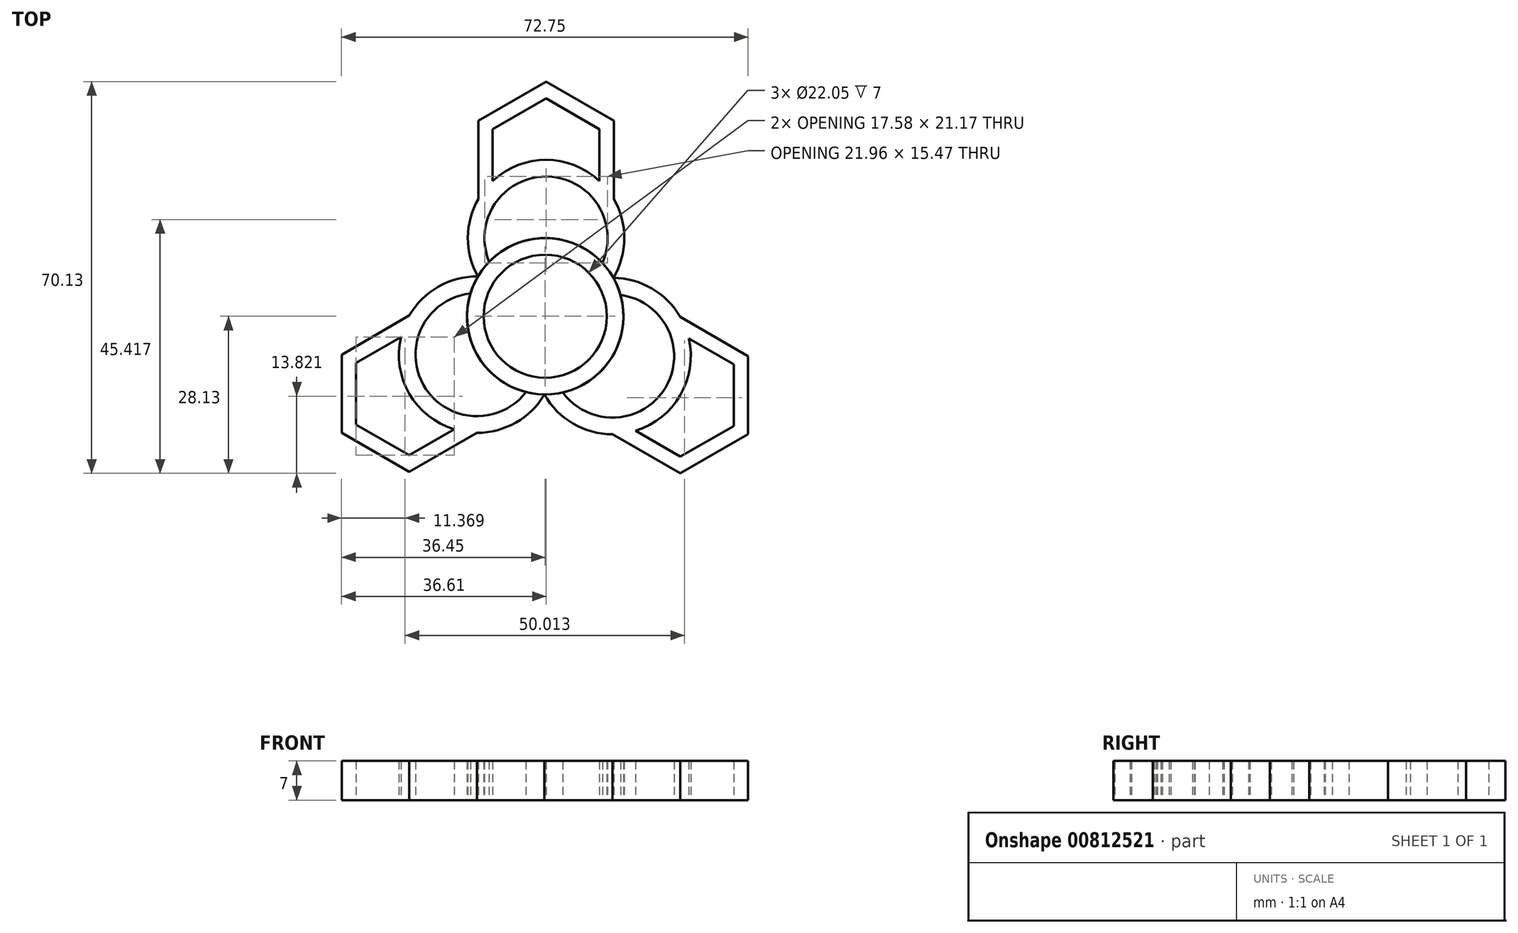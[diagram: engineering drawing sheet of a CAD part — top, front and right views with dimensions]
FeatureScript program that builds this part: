
annotation { "Feature Type Name" : "Feature", "Feature Type Description" : "" }
export const myFeature = defineFeature(function(context is Context, id is Id, definition is map)
    precondition{}
    {
        {
            var Q0;
            Q0=qCreatedBy(makeId("Top.planeOp"),FACE);
            var sketch = newSketch(context, id + "F0", { "sketchPlane" : qUnion([Q0])});
            skCircle(sketch, "E0", {"center": v(0, 0) * mm, "radius": 11.02 * mm});
            skCircle(sketch, "E1", {"center": v(0, 0) * mm, "radius": 14 * mm});
            skCircle(sketch, "E2", {"center": v(0.15, 14) * mm, "radius": 14 * mm});
            skCircle(sketch, "E3", {"center": v(0.15, 14) * mm, "radius": 11.02 * mm});
            skCircle(sketch, "E4.cCircle", {"center": v(0.15, 28) * mm, "radius": 14 * mm, "construction": true});
            skLineSegment(sketch, "E4.0", {"start": v(0.15, 14) * mm, "end": v(-11.98, 21) * mm});
            skLineSegment(sketch, "E4.1", {"start": v(-11.98, 21) * mm, "end": v(-11.98, 35) * mm});
            skLineSegment(sketch, "E4.2", {"start": v(-11.98, 35) * mm, "end": v(0.15, 42) * mm});
            skLineSegment(sketch, "E4.3", {"start": v(0.15, 42) * mm, "end": v(12.27, 35) * mm});
            skLineSegment(sketch, "E4.4", {"start": v(12.27, 35) * mm, "end": v(12.27, 21) * mm});
            skLineSegment(sketch, "E4.5", {"start": v(12.27, 21) * mm, "end": v(0.15, 14) * mm});
            skCircle(sketch, "E5.cCircle", {"center": v(0.15, 28) * mm, "radius": 11.02 * mm, "construction": true});
            skLineSegment(sketch, "E5.0", {"start": v(0.15, 39.02) * mm, "end": v(9.7, 33.51) * mm});
            skLineSegment(sketch, "E5.1", {"start": v(9.7, 33.51) * mm, "end": v(9.7, 22.49) * mm});
            skLineSegment(sketch, "E5.2", {"start": v(9.7, 22.49) * mm, "end": v(0.15, 16.98) * mm});
            skLineSegment(sketch, "E5.3", {"start": v(0.15, 16.98) * mm, "end": v(-9.4, 22.49) * mm});
            skLineSegment(sketch, "E5.4", {"start": v(-9.4, 22.49) * mm, "end": v(-9.4, 33.51) * mm});
            skLineSegment(sketch, "E5.5", {"start": v(-9.4, 33.51) * mm, "end": v(0.15, 39.02) * mm});
            skSolve(sketch);
        }
        {
            var Q0;
            {var subQ0=sQuery(id+"F0.wireOp",EDGE,"E2");var subQ1=sQuery(id+"F0.wireOp",EDGE,"E0");var subQ2=makeQuery(id+"F0.imprint","INTERSECT",VERTEX,{"disambiguationData":[OD(0.0)],"derivedFrom":[subQ1,subQ0]});Q0=makeQuery(id+"F0.imprint","IMPRINT",FACE,{"disambiguationData":[TD([[makeQuery(id+"F0.imprint","IMPRINT",EDGE,{"disambiguationData":[TD([[subQ2,1.0]])],"derivedFrom":subQ1}),-1.0]])]});}
            var Q1;
            {var subQ2=sQuery(id+"F0.wireOp",EDGE,"E3");var subQ4=sQuery(id+"F0.wireOp",EDGE,"E0");var subQ7=makeQuery(id+"F0.imprint","INTERSECT",VERTEX,{"disambiguationData":[OD(0.0)],"derivedFrom":[subQ4,subQ2]});Q1=makeQuery(id+"F0.imprint","IMPRINT",FACE,{"disambiguationData":[TD([[makeQuery(id+"F0.imprint","IMPRINT",EDGE,{"disambiguationData":[TD([[subQ7,-1.0]])],"derivedFrom":subQ4}),-1.0]])]});}
            var Q2;
            {var subQ0=sQuery(id+"F0.wireOp",EDGE,"E3");var subQ1=sQuery(id+"F0.wireOp",EDGE,"E0");var subQ2=makeQuery(id+"F0.imprint","INTERSECT",VERTEX,{"disambiguationData":[OD(1.0)],"derivedFrom":[subQ1,subQ0]});Q2=makeQuery(id+"F0.imprint","IMPRINT",FACE,{"disambiguationData":[TD([[makeQuery(id+"F0.imprint","IMPRINT",EDGE,{"disambiguationData":[TD([[subQ2,-1.0]])],"derivedFrom":subQ1}),-1.0]])]});}
            var Q3;
            {var subQ0=sQuery(id+"F0.wireOp",EDGE,"E3");var subQ1=sQuery(id+"F0.wireOp",EDGE,"E0");var subQ2=makeQuery(id+"F0.imprint","INTERSECT",VERTEX,{"disambiguationData":[OD(0.0)],"derivedFrom":[subQ1,subQ0]});Q3=makeQuery(id+"F0.imprint","IMPRINT",FACE,{"disambiguationData":[TD([[makeQuery(id+"F0.imprint","IMPRINT",EDGE,{"disambiguationData":[TD([[subQ2,1.0]])],"derivedFrom":subQ1}),-1.0]])]});}
            extrude(context, id + "F1", {"entities" : qUnion([Q0, Q1, Q2, Q3]), "depth" : 7 * mm, "offsetDistance" : 25.4 * mm});
        }
        {
            var Q0;
            {var subQ0=sQuery(id+"F0.wireOp",EDGE,"E2");var subQ1=sQuery(id+"F0.wireOp",EDGE,"E1");var subQ2=makeQuery(id+"F0.imprint","INTERSECT",VERTEX,{"disambiguationData":[OD(0.0)],"derivedFrom":[subQ1,subQ0]});Q0=makeQuery(id+"F0.imprint","IMPRINT",FACE,{"disambiguationData":[TD([[makeQuery(id+"F0.imprint","IMPRINT",EDGE,{"disambiguationData":[TD([[subQ2,-1.0]])],"derivedFrom":subQ1}),-1.0]])]});}
            var Q1;
            {var subQ0=sQuery(id+"F0.wireOp",EDGE,"E2");var subQ1=sQuery(id+"F0.wireOp",EDGE,"E1");var subQ2=makeQuery(id+"F0.imprint","INTERSECT",VERTEX,{"disambiguationData":[OD(1.0)],"derivedFrom":[subQ1,subQ0]});Q1=makeQuery(id+"F0.imprint","IMPRINT",FACE,{"disambiguationData":[TD([[makeQuery(id+"F0.imprint","IMPRINT",EDGE,{"disambiguationData":[TD([[subQ2,1.0]])],"derivedFrom":subQ1}),-1.0]])]});}
            extrude(context, id + "F2", {"entities" : qUnion([Q0, Q1]), "operationType" : NewBodyOperationType.ADD, "depth" : 7 * mm, "offsetDistance" : 25.4 * mm});
        }
        {
            var Q0;
            {var subQ0=sQuery(id+"F0.wireOp",EDGE,"E5.2");var subQ7=sQuery(id+"F0.wireOp",EDGE,"E3");var subQ9=makeQuery(id+"F0.imprint","INTERSECT",VERTEX,{"derivedFrom":[subQ7,subQ0]});Q0=makeQuery(id+"F0.imprint","IMPRINT",FACE,{"disambiguationData":[TD([[makeQuery(id+"F0.imprint","IMPRINT",EDGE,{"disambiguationData":[TD([[subQ9,1.0]])],"derivedFrom":subQ7}),-1.0]])]});}
            var Q1;
            {var subQ1=sQuery(id+"F0.wireOp",EDGE,"E5.3");var subQ3=sQuery(id+"F0.wireOp",EDGE,"E3");var subQ4=makeQuery(id+"F0.imprint","INTERSECT",VERTEX,{"derivedFrom":[subQ3,subQ1]});Q1=makeQuery(id+"F0.imprint","IMPRINT",FACE,{"disambiguationData":[TD([[makeQuery(id+"F0.imprint","IMPRINT",EDGE,{"disambiguationData":[TD([[subQ4,-1.0]])],"derivedFrom":subQ3}),-1.0]])]});}
            var Q2;
            {var subQ0=sQuery(id+"F0.wireOp",EDGE,"E4.1");Q2=makeQuery(id+"F0.imprint","IMPRINT",FACE,{"disambiguationData":[TD([[makeQuery(id+"F0.imprint","IMPRINT",EDGE,{"derivedFrom":subQ0}),-1.0]])]});}
            var Q3;
            {var subQ1=sQuery(id+"F0.wireOp",EDGE,"E5.1");var subQ9=sQuery(id+"F0.wireOp",EDGE,"E2");var subQ11=makeQuery(id+"F0.imprint","INTERSECT",VERTEX,{"derivedFrom":[subQ9,subQ1]});Q3=makeQuery(id+"F0.imprint","IMPRINT",FACE,{"disambiguationData":[TD([[makeQuery(id+"F0.imprint","IMPRINT",EDGE,{"disambiguationData":[TD([[subQ11,-1.0]])],"derivedFrom":subQ9}),1.0]])]});}
            extrude(context, id + "F3", {"entities" : qUnion([Q0, Q1, Q2, Q3]), "operationType" : NewBodyOperationType.ADD, "depth" : 7 * mm, "offsetDistance" : 25.4 * mm});
        }
        {
            var Q0;
            Q0=qCreatedBy(makeId("Front.planeOp"),FACE);
            var sketch = newSketch(context, id + "F4", { "sketchPlane" : qUnion([Q0])});
            skLineSegment(sketch, "E6", {"start": v(0, 0) * mm, "end": v(0, 22.64) * mm});
            skSolve(sketch);
        }
        {
            var Q0;
            Q0=makeQuery(id+"F1.opExtrude","SWEPT_BODY",BODY,{"disambiguationData":[OSD([sQuery(id+"F0.wireOp",EDGE,"E0"),sQuery(id+"F0.wireOp",EDGE,"E1")])]});
            var Q1;
            Q1=sQuery(id+"F4.wireOp",EDGE,"E6");
            circularPattern(context, id + "F5", {"entities" : qUnion([Q0]), "axis" : qUnion([Q1]), "angle" : 360 * degree, "instanceCount" : 3, "equalSpace" : true});
        }
    });
